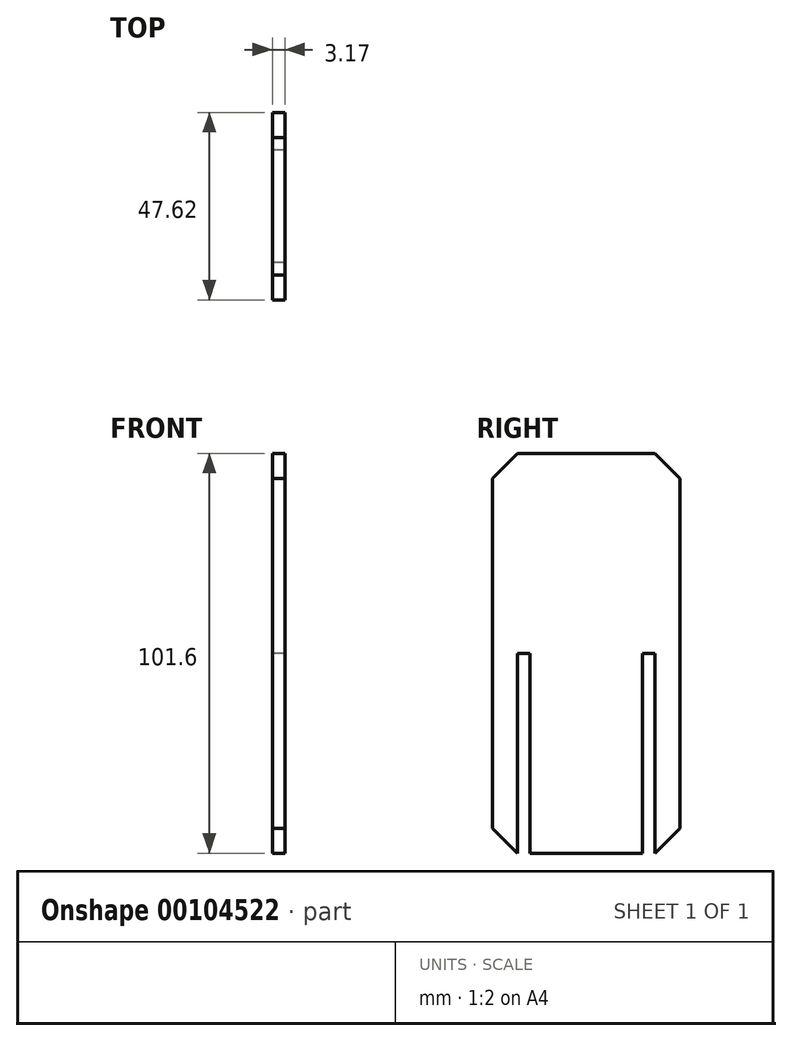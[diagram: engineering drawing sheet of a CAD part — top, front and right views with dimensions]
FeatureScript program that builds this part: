
annotation { "Feature Type Name" : "Feature", "Feature Type Description" : "" }
export const myFeature = defineFeature(function(context is Context, id is Id, definition is map)
    precondition{}
    {
        {
            var Q0;
            Q0=qCreatedBy(makeId("Right.planeOp"),FACE);
            var sketch = newSketch(context, id + "F0", { "sketchPlane" : qUnion([Q0])});
            skLineSegment(sketch, "E0.top", {"start": v(6.35, 101.6) * mm, "end": v(41.27, 101.6) * mm});
            skLineSegment(sketch, "E0.left", {"start": v(0, 6.35) * mm, "end": v(0, 95.25) * mm});
            skLineSegment(sketch, "E0.right", {"start": v(47.63, 6.35) * mm, "end": v(47.63, 95.25) * mm});
            skLineSegment(sketch, "E1.top", {"start": v(6.35, 50.8) * mm, "end": v(9.52, 50.8) * mm});
            skLineSegment(sketch, "E1.left", {"start": v(6.35, 0) * mm, "end": v(6.35, 50.8) * mm});
            skLineSegment(sketch, "E1.right", {"start": v(9.52, 0) * mm, "end": v(9.52, 50.8) * mm});
            skLineSegment(sketch, "E2.top", {"start": v(38.1, 50.8) * mm, "end": v(41.27, 50.8) * mm});
            skLineSegment(sketch, "E2.left", {"start": v(38.1, 0) * mm, "end": v(38.1, 50.8) * mm});
            skLineSegment(sketch, "E2.right", {"start": v(41.28, 0) * mm, "end": v(41.27, 50.8) * mm});
            skLineSegment(sketch, "E3.trimOffspring", {"start": v(9.52, 0) * mm, "end": v(38.1, 0) * mm});
            skPoint(sketch, "E4.start.orphan", {"position": v(3.17, 0) * mm});
            skPoint(sketch, "E5.start.orphan", {"position": v(44.45, 0) * mm});
            skLineSegment(sketch, "E6", {"start": v(6.35, 0) * mm, "end": v(0, 6.35) * mm});
            skLineSegment(sketch, "E7", {"start": v(41.28, 0) * mm, "end": v(47.62, 6.35) * mm});
            skPoint(sketch, "E8.orphan", {"position": v(0, 0) * mm});
            skPoint(sketch, "E9.orphan", {"position": v(47.63, 0) * mm});
            skLineSegment(sketch, "E10", {"start": v(6.35, 101.6) * mm, "end": v(0, 95.25) * mm});
            skLineSegment(sketch, "E11", {"start": v(41.27, 101.6) * mm, "end": v(47.62, 95.25) * mm});
            skSolve(sketch);
        }
        {
            var Q0;
            Q0 = qSketchRegion(id + "F0", true);
            extrude(context, id + "F1", {"entities" : qUnion([Q0]), "depth" : 3.17 * mm});
        }
    });
